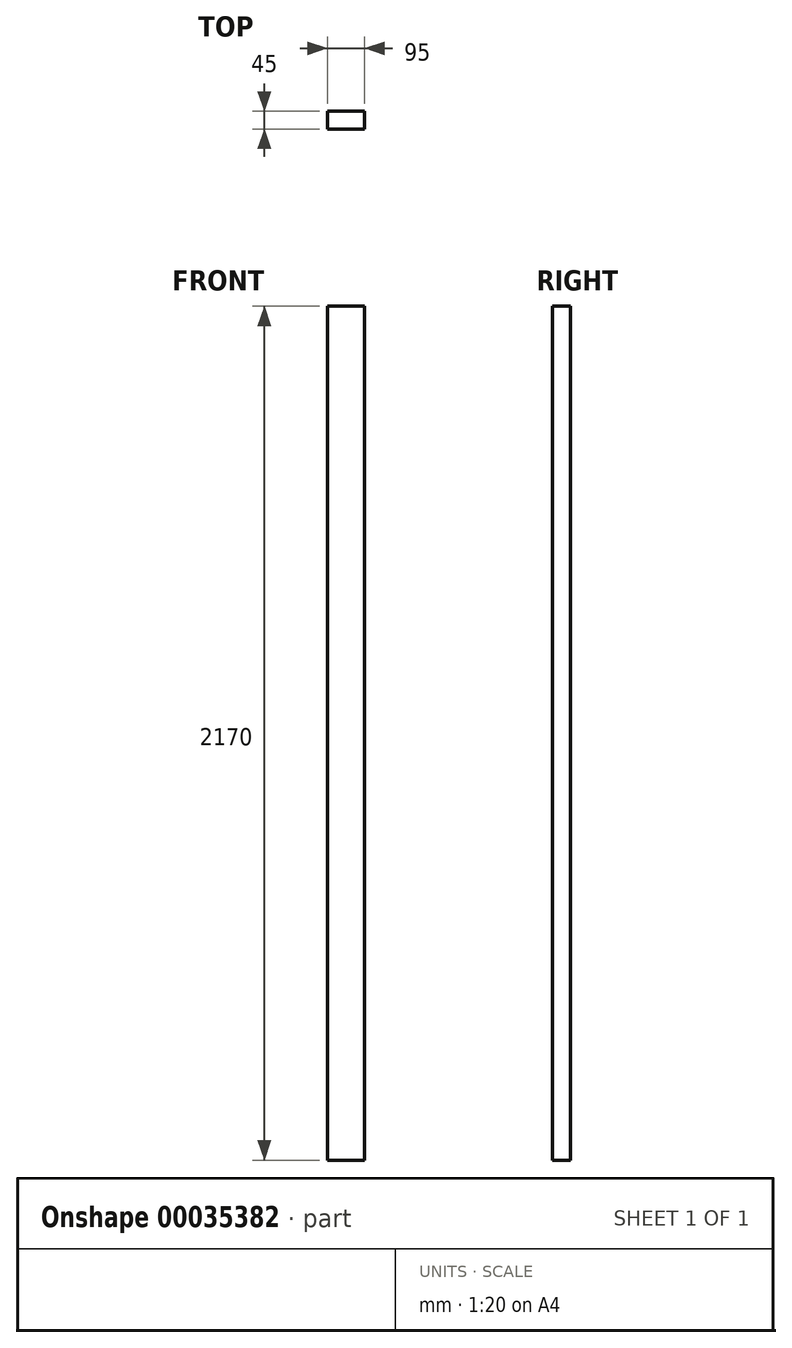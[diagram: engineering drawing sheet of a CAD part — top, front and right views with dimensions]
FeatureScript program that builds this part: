
annotation { "Feature Type Name" : "Feature", "Feature Type Description" : "" }
export const myFeature = defineFeature(function(context is Context, id is Id, definition is map)
    precondition{}
    {
        {
            var Q0;
            Q0=qCreatedBy(makeId("Top.planeOp"),FACE);
            var sketch = newSketch(context, id + "F0", { "sketchPlane" : qUnion([Q0])});
            skLineSegment(sketch, "E0.rect.bottom", {"start": v(47.5, -22.5) * mm, "end": v(-47.5, -22.5) * mm});
            skLineSegment(sketch, "E0.rect.top", {"start": v(47.5, 22.5) * mm, "end": v(-47.5, 22.5) * mm});
            skLineSegment(sketch, "E0.rect.left", {"start": v(47.5, -22.5) * mm, "end": v(47.5, 22.5) * mm});
            skLineSegment(sketch, "E0.rect.right", {"start": v(-47.5, -22.5) * mm, "end": v(-47.5, 22.5) * mm});
            skPoint(sketch, "E0.rect.middle", {"position": v(0, 0) * mm});
            skSolve(sketch);
        }
        {
            var Q0;
            Q0=makeQuery(id+"F0.imprint","IMPRINT",FACE,{"disambiguationData":[TD([[makeQuery(id+"F0.imprint","IMPRINT",EDGE,{"derivedFrom":sQuery(id+"F0.wireOp",EDGE,"E0.rect.bottom")}),-1.0]])]});
            extrude(context, id + "F1", {"entities" : qUnion([Q0]), "depth" : 2170 * mm});
        }
    });
